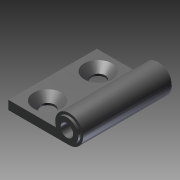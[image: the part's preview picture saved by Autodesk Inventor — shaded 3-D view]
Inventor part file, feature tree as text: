
AUTODESK INVENTOR PART (.ipt)
format: ipt  version: 2011 SP1 (Build 150282100, 282)  size: 124,928 bytes
history: native  units: mm
features: other x35, sketch x5, hole x3, revolve x1, extrude x1
ambient origin geometry x8: Origin, YZ Plane, XZ Plane, XY Plane, X Axis, Y Axis, Z Axis, Center Point
bodies: Solid1 (feature_tree)
feature tree (45):
  revolve  "Revolution1"  [1 undecoded]
  extrude  "Extrusion1"  TaperAngle=0.0deg  [1 undecoded]
  hole  "Hole1"  [1 undecoded]
  hole  "Hole2"  [1 undecoded]
  hole  "Hole3"  [1 undecoded]
  other  "2_XY"
  other  "2_YZ"
  other  "2_ZX"
  other  "2_X"
  other  "2_Y"
  other  "2_Z"
  other  "2_Center"
  other  "to_bolt3_XY"
  other  "to_bolt3_YZ"
  other  "to_bolt3_ZX"
  other  "to_bolt3_X"
  other  "to_bolt3_Y"
  other  "to_bolt3_Z"
  other  "to_bolt3_Center"
  other  "to_bolt3_r_XY"
  other  "to_bolt3_r_YZ"
  other  "to_bolt3_r_ZX"
  other  "to_bolt3_r_X"
  other  "to_bolt3_r_Y"
  other  "to_bolt3_r_Z"
  other  "to_bolt3_r_Center"
  other  "to_bolt4_XY"
  other  "to_bolt4_YZ"
  other  "to_bolt4_ZX"
  other  "to_bolt4_X"
  other  "to_bolt4_Y"
  other  "to_bolt4_Z"
  other  "to_bolt4_Center"
  other  "to_bolt4_r_XY"
  other  "to_bolt4_r_YZ"
  other  "to_bolt4_r_ZX"
  other  "to_bolt4_r_X"
  other  "to_bolt4_r_Y"
  other  "to_bolt4_r_Z"
  other  "to_bolt4_r_Center"
  sketch  "Sketch_1"  dims[d0=360.0deg d1=3.5mm d2=0.0mm]
  sketch  "Sketch_2"  dims[d3=5.5mm d4=6.0mm d5=11.0mm d6=2.0mm d7=90.0deg d8=3.5mm d9=0.0mm]
  sketch  "Sketch3"  dims[d10=5.5mm d11=6.0mm d12=11.0mm d13=2.0mm d14=90.0deg d15=3.5mm d16=0.0mm]
  sketch  "Sketch4"  dims[d17=5.0mm d18=6.0mm d19=4.0mm d20=2.0mm d21=90.0deg d22=36.8mm d23=0.0mm d24=0.0mm d25=0.0mm d26=0.0mm]
  sketch  "Sketch5"
note: 5 required parameter values undecoded (feature->parameter linkage not recoverable at this tier; creation-order binding heuristic only, values carry confidence <= 0.55)